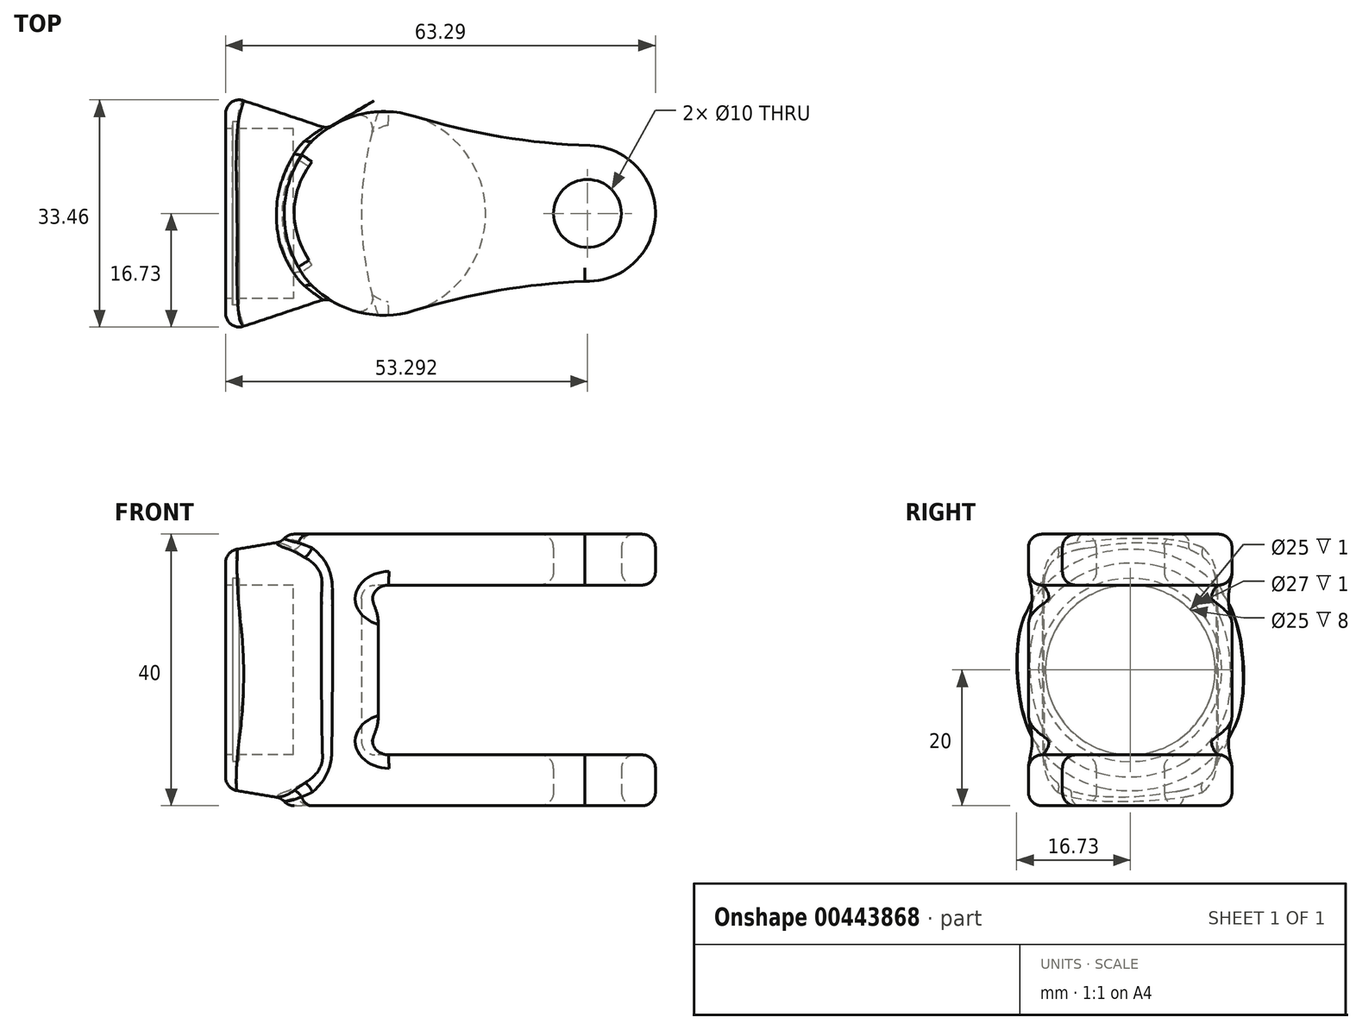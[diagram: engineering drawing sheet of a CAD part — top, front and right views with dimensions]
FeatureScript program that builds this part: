
annotation { "Feature Type Name" : "Feature", "Feature Type Description" : "" }
export const myFeature = defineFeature(function(context is Context, id is Id, definition is map)
    precondition{}
    {
        {
            var Q0;
            Q0=qCreatedBy(makeId("Right.planeOp"),FACE);
            var sketch = newSketch(context, id + "F0", { "sketchPlane" : qUnion([Q0])});
            skCircle(sketch, "E0", {"center": v(0, 0) * mm, "radius": 17.5 * mm});
            skSolve(sketch);
        }
        {
            var Q0;
            Q0=qCreatedBy(makeId("Right.planeOp"),FACE);
            cPlane(context, id + "F1", {"entities" : qUnion([Q0]), "cplaneType" : CPlaneType.OFFSET, "offset" : 15 * mm, "width" : 150 * mm, "height" : 150 * mm});
        }
        {
            var Q0;
            Q0=qCreatedBy(id+"F1.planeOp",FACE);
            var sketch = newSketch(context, id + "F2", { "sketchPlane" : qUnion([Q0])});
            skLineSegment(sketch, "E1.bottom", {"start": v(5, 20) * mm, "end": v(-5, 20) * mm});
            skLineSegment(sketch, "E1.top", {"start": v(5, -20) * mm, "end": v(-5, -20) * mm});
            skLineSegment(sketch, "E1.left", {"start": v(12.5, 12.5) * mm, "end": v(12.5, -12.5) * mm});
            skLineSegment(sketch, "E1.right", {"start": v(-12.5, 12.5) * mm, "end": v(-12.5, -12.5) * mm});
            skPoint(sketch, "E1.middle", {"position": v(0, 0) * mm});
            skPoint(sketch, "E2.visualSharp", {"position": v(-12.5, 20) * mm});
            skArc(sketch, "E2.filletArc", {"start": v(-5, 20) * mm, "mid": v(-10.3, 17.8) * mm, "end": v(-12.5, 12.5) * mm});
            skPoint(sketch, "E3.visualSharp", {"position": v(12.5, 20) * mm});
            skArc(sketch, "E3.filletArc", {"start": v(12.5, 12.5) * mm, "mid": v(10.3, 17.8) * mm, "end": v(5, 20) * mm});
            skPoint(sketch, "E4.visualSharp", {"position": v(-12.5, -20) * mm});
            skArc(sketch, "E4.filletArc", {"start": v(-12.5, -12.5) * mm, "mid": v(-10.3, -17.8) * mm, "end": v(-5, -20) * mm});
            skPoint(sketch, "E5.visualSharp", {"position": v(12.5, -20) * mm});
            skArc(sketch, "E5.filletArc", {"start": v(5, -20) * mm, "mid": v(10.3, -17.8) * mm, "end": v(12.5, -12.5) * mm});
            skSolve(sketch);
        }
        {
            var Q0;
            Q0=makeQuery(id+"F2.imprint","IMPRINT",FACE,{"disambiguationData":[TD([[makeQuery(id+"F2.imprint","IMPRINT",EDGE,{"derivedFrom":sQuery(id+"F2.wireOp",EDGE,"E1.bottom")}),1.0]])]});
            var Q1;
            Q1=makeQuery(id+"F0.imprint","IMPRINT",FACE,{"disambiguationData":[TD([[makeQuery(id+"F0.imprint","IMPRINT",EDGE,{"derivedFrom":sQuery(id+"F0.wireOp",EDGE,"E0")}),1.0]])]});
            loft(context, id + "F3", {"sheetProfilesArray" : [{ "sheetProfileEntities" : qUnion([Q0]) }, { "sheetProfileEntities" : qUnion([Q1]) }]});
        }
        {
            var Q0;
            Q0=qCreatedBy(makeId("Top.planeOp"),FACE);
            var sketch = newSketch(context, id + "F4", { "sketchPlane" : qUnion([Q0])});
            skArc(sketch, "E6", {"start": v(27.7, 14.34) * mm, "mid": v(8.3, 0) * mm, "end": v(27.7, -14.34) * mm});
            skArc(sketch, "E7", {"start": v(52.92, -10) * mm, "mid": v(63.29, -0.36) * mm, "end": v(53.63, 10) * mm});
            skArc(sketch, "E8", {"start": v(27.7, 14.34) * mm, "mid": v(40.52, 11.31) * mm, "end": v(53.63, 10) * mm});
            skArc(sketch, "E9", {"start": v(52.92, -10) * mm, "mid": v(40.18, -11.35) * mm, "end": v(27.7, -14.34) * mm});
            skLineSegment(sketch, "E10", {"start": v(23.3, 0) * mm, "end": v(53.3, 0) * mm, "construction": true});
            skSolve(sketch);
        }
        {
            var Q0;
            Q0=makeQuery(id+"F4.imprint","IMPRINT",FACE,{"disambiguationData":[TD([[makeQuery(id+"F4.imprint","IMPRINT",EDGE,{"derivedFrom":sQuery(id+"F4.wireOp",EDGE,"E6")}),1.0]])]});
            extrude(context, id + "F5", {"entities" : qUnion([Q0]), "operationType" : NewBodyOperationType.ADD, "endBound" : BoundingType.SYMMETRIC, "depth" : 40 * mm});
        }
        {
            var Q0;
            Q0=qCreatedBy(makeId("Front.planeOp"),FACE);
            var sketch = newSketch(context, id + "F6", { "sketchPlane" : qUnion([Q0])});
            skLineSegment(sketch, "E11.bottom", {"start": v(20, 12.5) * mm, "end": v(66.32, 12.5) * mm});
            skLineSegment(sketch, "E11.top", {"start": v(20, -12.5) * mm, "end": v(66.32, -12.5) * mm});
            skLineSegment(sketch, "E11.left", {"start": v(20, 12.5) * mm, "end": v(20, -12.5) * mm});
            skLineSegment(sketch, "E11.right", {"start": v(66.32, 12.5) * mm, "end": v(66.32, -12.5) * mm});
            skSolve(sketch);
        }
        {
            var Q0;
            Q0 = qSketchRegion(id + "F6", true);
            var Q1;
            Q1=sQuery(id+"F6.wireOp",EDGE,"E11.right");
            revolve(context, id + "F7", {"operationType" : NewBodyOperationType.REMOVE, "entities" : qUnion([Q0]), "axis" : qUnion([Q1]), "revolveType" : RevolveType.FULL, "oppositeDirection" : true});
        }
        {
            var Q0;
            Q0=qCreatedBy(makeId("Right.planeOp"),FACE);
            var sketch = newSketch(context, id + "F8", { "sketchPlane" : qUnion([Q0])});
            skCircle(sketch, "E12", {"center": v(0, 0) * mm, "radius": 12.5 * mm});
            skSolve(sketch);
        }
        {
            var Q0;
            Q0=makeQuery(id+"F8.imprint","IMPRINT",FACE,{"disambiguationData":[TD([[makeQuery(id+"F8.imprint","IMPRINT",EDGE,{"derivedFrom":sQuery(id+"F8.wireOp",EDGE,"E12")}),1.0]])]});
            extrude(context, id + "F9", {"entities" : qUnion([Q0]), "operationType" : NewBodyOperationType.REMOVE, "depth" : 10 * mm});
        }
        {
            var Q0;
            Q0=makeQuery(id+"F3.opLoft","CAP_FACE",FACE,{"disambiguationData":[OSD([makeQuery(id+"F0.imprint","IMPRINT",FACE,{"disambiguationData":[TD([[makeQuery(id+"F0.imprint","IMPRINT",EDGE,{"derivedFrom":sQuery(id+"F0.wireOp",EDGE,"E0")}),1.0]])]})])],"isStart":true});
            cPlane(context, id + "F10", {"entities" : qUnion([Q0]), "cplaneType" : CPlaneType.OFFSET, "offset" : 1 * mm, "oppositeDirection" : true, "width" : 150 * mm, "height" : 150 * mm});
        }
        {
            var Q0;
            Q0=qCreatedBy(id+"F10.planeOp",FACE);
            var sketch = newSketch(context, id + "F11", { "sketchPlane" : qUnion([Q0])});
            skCircle(sketch, "E13.0", {"center": v(0, 0) * mm, "radius": 13.5 * mm});
            skSolve(sketch);
        }
        {
            var Q0;
            Q0=makeQuery(id+"F11.imprint","IMPRINT",FACE,{"disambiguationData":[TD([[makeQuery(id+"F11.imprint","IMPRINT",EDGE,{"derivedFrom":sQuery(id+"F11.wireOp",EDGE,"E13.0")}),1.0]])]});
            var Q1;
            Q1=sQuery(id+"F11.wireOp",EDGE,"E13.0");
            extrude(context, id + "F12", {"entities" : qUnion([Q0]), "operationType" : NewBodyOperationType.REMOVE, "surfaceEntities" : qUnion([Q1]), "oppositeDirection" : true, "depth" : 1 * mm});
        }
        {
            var Q0;
            Q0=makeQuery(id+"F5.opExtrude","CAP_FACE",FACE,{"disambiguationData":[OSD([sQuery(id+"F4.wireOp",EDGE,"E6"),sQuery(id+"F4.wireOp",EDGE,"E7"),sQuery(id+"F4.wireOp",EDGE,"E8"),sQuery(id+"F4.wireOp",EDGE,"E9")])],"isStart":true});
            var sketch = newSketch(context, id + "F13", { "sketchPlane" : qUnion([Q0])});
            skCircle(sketch, "E14", {"center": v(53.3, 0) * mm, "radius": 5 * mm});
            skSolve(sketch);
        }
        {
            var Q0;
            Q0 = qSketchRegion(id + "F13", true);
            extrude(context, id + "F14", {"entities" : qUnion([Q0]), "operationType" : NewBodyOperationType.REMOVE, "endBound" : BoundingType.THROUGH_ALL, "oppositeDirection" : true, "depth" : 25 * mm});
        }
        {
            var Q0;
            Q0=makeQuery(id+"F5.opExtrude","CAP_FACE",FACE,{"disambiguationData":[OSD([sQuery(id+"F4.wireOp",EDGE,"E6"),sQuery(id+"F4.wireOp",EDGE,"E7"),sQuery(id+"F4.wireOp",EDGE,"E8"),sQuery(id+"F4.wireOp",EDGE,"E9")])],"isStart":true});
            var Q1;
            Q1=makeQuery(id+"F5.opExtrude","CAP_FACE",FACE,{"disambiguationData":[OSD([sQuery(id+"F4.wireOp",EDGE,"E6"),sQuery(id+"F4.wireOp",EDGE,"E7"),sQuery(id+"F4.wireOp",EDGE,"E8"),sQuery(id+"F4.wireOp",EDGE,"E9")])],"isStart":false});
            var Q2;
            Q2=makeQuery(id+"F7.boolean.opBoolean","COPY",FACE,{"derivedFrom":makeQuery(id+"F7.opRevolve","SWEPT_FACE",FACE,{"disambiguationData":[OSD([sQuery(id+"F6.wireOp",EDGE,"E11.bottom")])]})});
            var Q3;
            Q3=makeQuery(id+"F7.boolean.opBoolean","COPY",FACE,{"derivedFrom":makeQuery(id+"F7.opRevolve","SWEPT_FACE",FACE,{"disambiguationData":[OSD([sQuery(id+"F6.wireOp",EDGE,"E11.top")])]})});
            var Q4;
            Q4=makeQuery(id+"F7.boolean.opBoolean","COPY",EDGE,{"derivedFrom":makeQuery(id+"F7.opRevolve","SWEPT_EDGE",EDGE,{"disambiguationData":[OSD([sQuery(id+"F6.wireOp",EDGE,"E11.top"),sQuery(id+"F6.wireOp",EDGE,"E11.left")])]})});
            var Q5;
            Q5=makeQuery(id+"F7.boolean.opBoolean","COPY",EDGE,{"derivedFrom":makeQuery(id+"F7.opRevolve","SWEPT_EDGE",EDGE,{"disambiguationData":[OSD([sQuery(id+"F6.wireOp",EDGE,"E11.bottom"),sQuery(id+"F6.wireOp",EDGE,"E11.left")])]})});
            fillet(context, id + "F15", {"entities" : qUnion([Q0, Q1, Q2, Q3, Q4, Q5]), "radius" : 2 * mm, "tangentPropagation" : true, "allowEdgeOverflow" : false});
        }
        {
            var Q0;
            Q0=makeQuery(id+"F3.opLoft","SWEPT_FACE",FACE,{"disambiguationData":[OSD([sQuery(id+"F0.wireOp",EDGE,"E0"),sQuery(id+"F2.wireOp",EDGE,"E1.bottom"),sQuery(id+"F2.wireOp",EDGE,"E1.left"),sQuery(id+"F2.wireOp",EDGE,"E3.filletArc")])]});
            fillet(context, id + "F16", {"entities" : qUnion([Q0]), "radius" : 2 * mm, "tangentPropagation" : true, "allowEdgeOverflow" : false});
        }
    });
